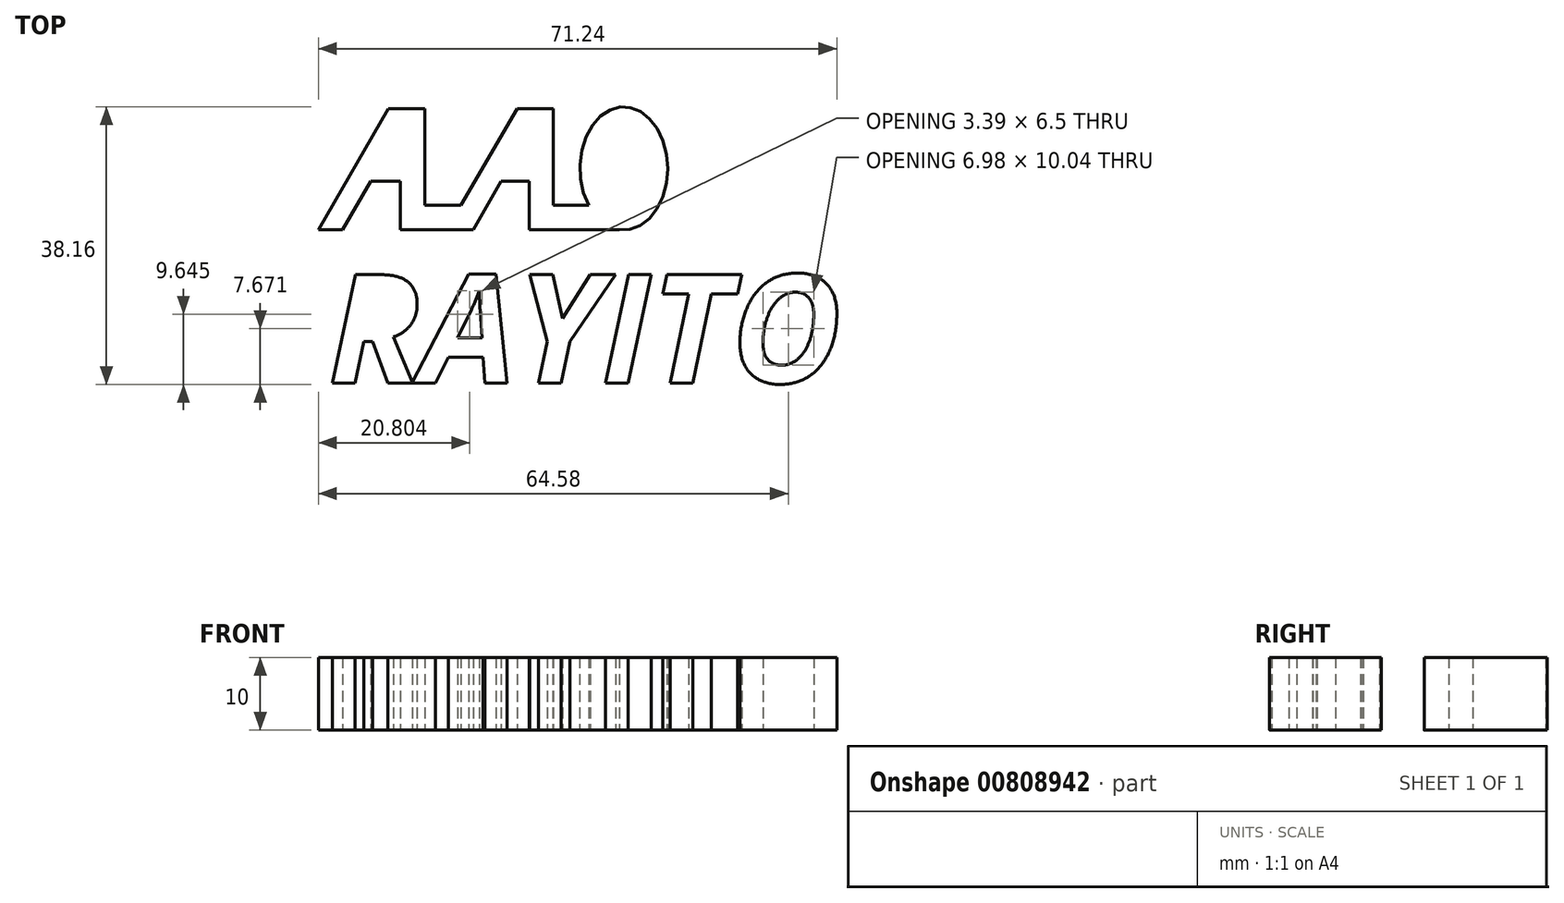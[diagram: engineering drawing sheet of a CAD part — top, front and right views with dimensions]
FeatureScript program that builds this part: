
annotation { "Feature Type Name" : "Feature", "Feature Type Description" : "" }
export const myFeature = defineFeature(function(context is Context, id is Id, definition is map)
    precondition{}
    {
        {
            var Q0;
            Q0=qCreatedBy(makeId("Top.planeOp"),FACE);
            var sketch = newSketch(context, id + "F0", { "sketchPlane" : qUnion([Q0])});
            skLineSegment(sketch, "E0", {"start": v(-11.68, 16.64) * mm, "end": v(-6.7, 16.64) * mm});
            skLineSegment(sketch, "E1", {"start": v(-6.7, 16.64) * mm, "end": v(-6.7, 3.33) * mm});
            skLineSegment(sketch, "E2", {"start": v(-6.7, 3.33) * mm, "end": v(-1.7, 3.33) * mm});
            skLineSegment(sketch, "E3", {"start": v(-1.7, 3.33) * mm, "end": v(6, 16.64) * mm});
            skLineSegment(sketch, "E4", {"start": v(6, 16.64) * mm, "end": v(11, 16.64) * mm});
            skLineSegment(sketch, "E5", {"start": v(11, 16.64) * mm, "end": v(11, 3.33) * mm});
            skLineSegment(sketch, "E6", {"start": v(7.66, 0) * mm, "end": v(7.66, 6.67) * mm});
            skLineSegment(sketch, "E7", {"start": v(7.66, 6.67) * mm, "end": v(3.81, 6.67) * mm});
            skLineSegment(sketch, "E8", {"start": v(3.81, 6.67) * mm, "end": v(-0.03, 0) * mm});
            skLineSegment(sketch, "E9", {"start": v(-0.03, 0) * mm, "end": v(-10.03, 0) * mm});
            skLineSegment(sketch, "E10", {"start": v(-10.03, 0) * mm, "end": v(-10.03, 6.67) * mm});
            skLineSegment(sketch, "E11", {"start": v(-10.03, 6.67) * mm, "end": v(-14.11, 6.67) * mm});
            skLineSegment(sketch, "E12", {"start": v(-14.11, 6.67) * mm, "end": v(-17.96, 0) * mm});
            skLineSegment(sketch, "E13", {"start": v(-17.96, 0) * mm, "end": v(-21.3, 0) * mm});
            skLineSegment(sketch, "E14", {"start": v(-21.3, 0) * mm, "end": v(-11.68, 16.64) * mm});
            skEllipticalArc(sketch, "E15", {});
            skLineSegment(sketch, "E16", {"start": v(11, 3.33) * mm, "end": v(15.83, 3.33) * mm});
            skLineSegment(sketch, "E17", {"start": v(20.09, 0) * mm, "end": v(7.66, 0) * mm});
            const initialGuessF0  = {"E15": [0.020659204617632872, 0.008421080654537661, 0, -1, 0.008459144940475014, 0.006042246386053581, 6.188283693918039, 5.358133066516751]};
            skSetInitialGuess(sketch, initialGuessF0);
            skSolve(sketch);
        }
        {
            var Q0;
            Q0=makeQuery(id+"F0.imprint","IMPRINT",FACE,{"disambiguationData":[TD([[makeQuery(id+"F0.imprint","IMPRINT",EDGE,{"derivedFrom":sQuery(id+"F0.wireOp",EDGE,"E0")}),-1.0]])]});
            extrude(context, id + "F1", {"entities" : qUnion([Q0]), "depth" : 10 * mm, "offsetDistance" : 25 * mm});
        }
        {
            var Q0;
            Q0=qCreatedBy(makeId("Top.planeOp"),FACE);
            var sketch = newSketch(context, id + "F2", { "sketchPlane" : qUnion([Q0])});
            skText(sketch, "E18", { "text": "RAYITO", "fontName": "OpenSans-BoldItalic.ttf"});
            const initialGuessF2  = {"E18": [-0.0199, -0.02107, 1, 0, 0.015]};
            skSetInitialGuess(sketch, initialGuessF2);
            skSolve(sketch);
        }
        {
            var Q0;
            Q0 = qSketchRegion(id + "F2", true);
            var Q1;
            Q1=makeQuery(id+"F2.imprint","IMPRINT",FACE,{"disambiguationData":[TD([[makeQuery(id+"F2.imprint","IMPRINT",EDGE,{"derivedFrom":sQuery(id+"F2.wireOp",EDGE,"E18.sketch_text.stroke-0")}),1.0]])]});
            var Q2;
            Q2=makeQuery(id+"F2.imprint","IMPRINT",FACE,{"disambiguationData":[TD([[makeQuery(id+"F2.imprint","IMPRINT",EDGE,{"derivedFrom":sQuery(id+"F2.wireOp",EDGE,"E18.sketch_text.stroke-0")}),-1.0]])]});
            extrude(context, id + "F3", {"entities" : qUnion([Q0, Q1, Q2]), "depth" : 10 * mm, "offsetDistance" : 25 * mm});
        }
    });
